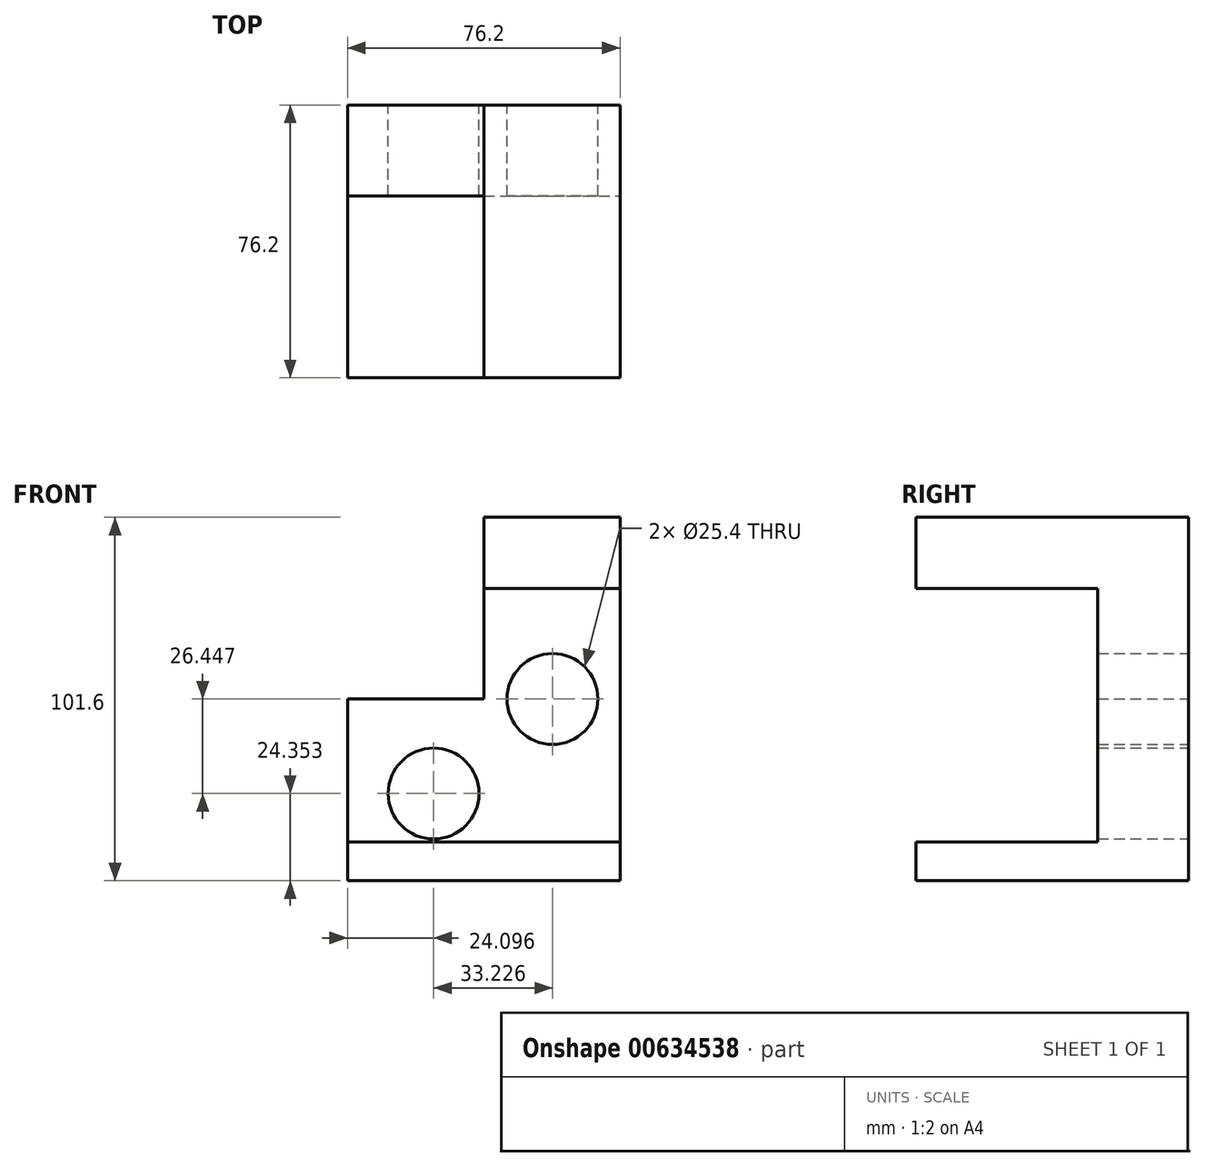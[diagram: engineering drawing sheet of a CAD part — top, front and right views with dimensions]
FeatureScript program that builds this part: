
annotation { "Feature Type Name" : "Feature", "Feature Type Description" : "" }
export const myFeature = defineFeature(function(context is Context, id is Id, definition is map)
    precondition{}
    {
        {
            var Q0;
            Q0=qCreatedBy(makeId("Front.planeOp"),FACE);
            var sketch = newSketch(context, id + "F0", { "sketchPlane" : qUnion([Q0])});
            skLineSegment(sketch, "E0", {"start": v(22.3, 50.8) * mm, "end": v(22.3, 0) * mm});
            skLineSegment(sketch, "E1", {"start": v(22.3, 0) * mm, "end": v(-15.8, 0) * mm});
            skLineSegment(sketch, "E2", {"start": v(-15.8, 0) * mm, "end": v(-15.8, -50.8) * mm});
            skLineSegment(sketch, "E3", {"start": v(-15.8, -50.8) * mm, "end": v(60.4, -50.8) * mm});
            skLineSegment(sketch, "E4", {"start": v(60.4, -50.8) * mm, "end": v(60.4, 0) * mm});
            skLineSegment(sketch, "E5", {"start": v(60.4, 0) * mm, "end": v(60.4, 50.8) * mm});
            skLineSegment(sketch, "E6", {"start": v(22.3, 50.8) * mm, "end": v(60.4, 50.8) * mm});
            skCircle(sketch, "E7", {"center": v(8.3, -26.45) * mm, "radius": 12.7 * mm});
            skCircle(sketch, "E8", {"center": v(41.53, 0) * mm, "radius": 12.7 * mm});
            skLineSegment(sketch, "E9", {"start": v(-15.8, -40) * mm, "end": v(60.4, -40) * mm});
            skLineSegment(sketch, "E10", {"start": v(22.3, 30.84) * mm, "end": v(60.4, 30.84) * mm});
            skSolve(sketch);
        }
        {
            var Q0;
            {var subQ1=sQuery(id+"F0.wireOp",EDGE,"E1");Q0=makeQuery(id+"F0.imprint","IMPRINT",FACE,{"disambiguationData":[TD([[makeQuery(id+"F0.imprint","IMPRINT",EDGE,{"derivedFrom":subQ1}),1.0]])]});}
            extrude(context, id + "F1", {"entities" : qUnion([Q0]), "depth" : 25.4 * mm, "offsetDistance" : 25.4 * mm});
        }
        {
            var Q0;
            {var subQ0=sQuery(id+"F0.wireOp",EDGE,"E6");Q0=makeQuery(id+"F0.imprint","IMPRINT",FACE,{"disambiguationData":[TD([[makeQuery(id+"F0.imprint","IMPRINT",EDGE,{"derivedFrom":subQ0}),-1.0]])]});}
            var Q1;
            {var subQ0=sQuery(id+"F0.wireOp",EDGE,"E3");Q1=makeQuery(id+"F0.imprint","IMPRINT",FACE,{"disambiguationData":[TD([[makeQuery(id+"F0.imprint","IMPRINT",EDGE,{"derivedFrom":subQ0}),1.0]])]});}
            extrude(context, id + "F2", {"entities" : qUnion([Q0, Q1]), "operationType" : NewBodyOperationType.ADD, "depth" : 76.2 * mm, "offsetDistance" : 25.4 * mm});
        }
    });
